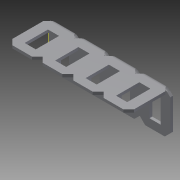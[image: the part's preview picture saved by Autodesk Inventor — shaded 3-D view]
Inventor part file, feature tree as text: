
AUTODESK INVENTOR PART (.ipt)
format: ipt  version: 2012 (Build 160160000, 160)  size: 555,520 bytes
history: native  units: in
note: dims shown in document units (in); Inventor stores cm internally (conversion verified against a paired STEP export)
features: other x1, imported_body x1, plane x1, split x1
ambient origin geometry x8: Origin, YZ Plane, XZ Plane, XY Plane, X Axis, Y Axis, Z Axis, Center Point
feature tree (4):
  parser-record x1  (decoder bookkeeping rows leaked as tree rows — omitted from the tree; the rows remain in map.json)
  imported_body  "Base1"
  plane  "Work Plane1"
  split  "Split1"
